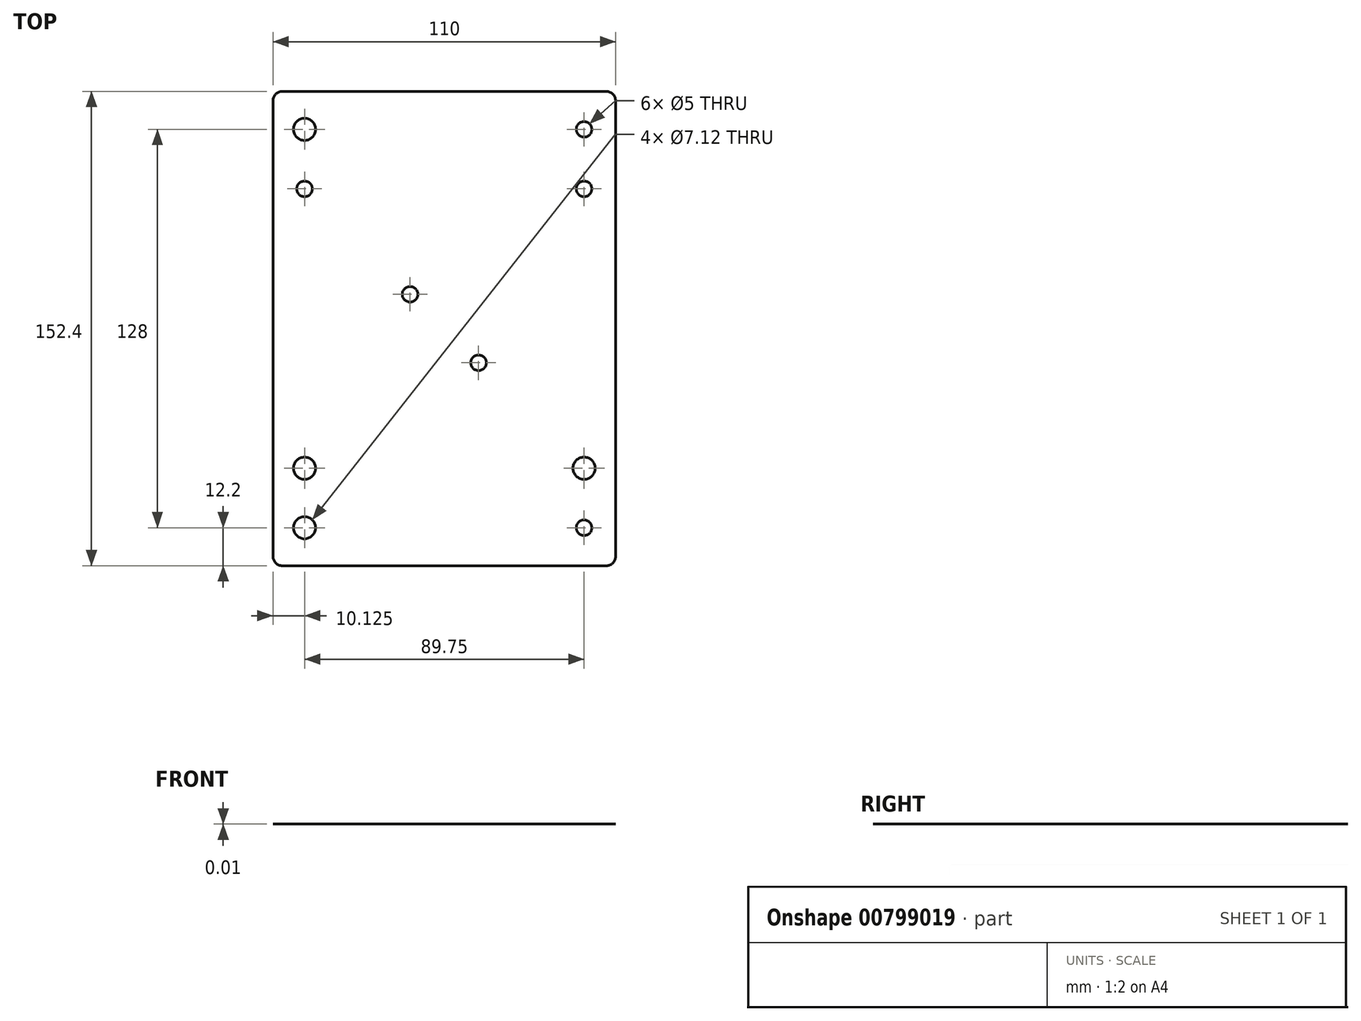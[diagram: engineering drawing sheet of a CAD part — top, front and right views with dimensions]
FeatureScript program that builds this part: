
annotation { "Feature Type Name" : "Feature", "Feature Type Description" : "" }
export const myFeature = defineFeature(function(context is Context, id is Id, definition is map)
    precondition{}
    {
        {
            var Q0;
            Q0=qCreatedBy(makeId("Top.planeOp"),FACE);
            var sketch = newSketch(context, id + "F0", { "sketchPlane" : qUnion([Q0])});
            skCircle(sketch, "E0", {"center": v(-11, 11) * mm, "radius": 2.5 * mm});
            skCircle(sketch, "E1", {"center": v(-44.87, 44.88) * mm, "radius": 2.5 * mm});
            skCircle(sketch, "E2", {"center": v(-44.87, -44.88) * mm, "radius": 3.56 * mm});
            skCircle(sketch, "E3", {"center": v(44.88, 64) * mm, "radius": 2.5 * mm});
            skCircle(sketch, "E4", {"center": v(-44.88, 64) * mm, "radius": 3.56 * mm});
            skLineSegment(sketch, "E5", {"start": v(52, 76.2) * mm, "end": v(-52, 76.2) * mm});
            skArc(sketch, "E6", {"start": v(-52, 76.2) * mm, "mid": v(-54.12, 75.32) * mm, "end": v(-55, 73.2) * mm});
            skLineSegment(sketch, "E7", {"start": v(-55, 73.2) * mm, "end": v(-55, -73.2) * mm});
            skArc(sketch, "E8", {"start": v(-55, -73.2) * mm, "mid": v(-54.12, -75.32) * mm, "end": v(-52, -76.2) * mm});
            skLineSegment(sketch, "E9", {"start": v(-52, -76.2) * mm, "end": v(52, -76.2) * mm});
            skArc(sketch, "E10", {"start": v(52, -76.2) * mm, "mid": v(54.12, -75.32) * mm, "end": v(55, -73.2) * mm});
            skLineSegment(sketch, "E11", {"start": v(55, -73.2) * mm, "end": v(55, 73.2) * mm});
            skArc(sketch, "E12", {"start": v(55, 73.2) * mm, "mid": v(54.12, 75.32) * mm, "end": v(52, 76.2) * mm});
            skCircle(sketch, "E13", {"center": v(-44.87, -64) * mm, "radius": 3.56 * mm});
            skCircle(sketch, "E14", {"center": v(44.88, -64) * mm, "radius": 2.5 * mm});
            skCircle(sketch, "E15", {"center": v(44.88, -44.88) * mm, "radius": 3.56 * mm});
            skCircle(sketch, "E16", {"center": v(44.88, 44.88) * mm, "radius": 2.5 * mm});
            skCircle(sketch, "E17", {"center": v(11, -11) * mm, "radius": 2.5 * mm});
            skLineSegment(sketch, "E18", {"start": v(-44.88, 64) * mm, "end": v(-44.87, 44.88) * mm, "construction": true});
            skLineSegment(sketch, "E19", {"start": v(-44.87, -44.88) * mm, "end": v(-44.87, 44.88) * mm, "construction": true});
            skLineSegment(sketch, "E20", {"start": v(-44.87, -44.88) * mm, "end": v(-44.87, -64) * mm, "construction": true});
            skLineSegment(sketch, "E21", {"start": v(-44.87, -64) * mm, "end": v(-44.87, -76.2) * mm, "construction": true});
            skLineSegment(sketch, "E22", {"start": v(-44.88, 64) * mm, "end": v(-44.88, 76.2) * mm, "construction": true});
            skLineSegment(sketch, "E23", {"start": v(44.88, 44.88) * mm, "end": v(44.88, -44.88) * mm, "construction": true});
            skLineSegment(sketch, "E24", {"start": v(44.88, -64) * mm, "end": v(44.88, -44.88) * mm, "construction": true});
            skLineSegment(sketch, "E25", {"start": v(44.88, -64) * mm, "end": v(44.88, -76.2) * mm, "construction": true});
            skLineSegment(sketch, "E26", {"start": v(-44.87, -64) * mm, "end": v(44.88, -64) * mm, "construction": true});
            skLineSegment(sketch, "E27", {"start": v(44.88, -64) * mm, "end": v(55, -64) * mm, "construction": true});
            skLineSegment(sketch, "E28", {"start": v(-44.87, -64) * mm, "end": v(-55, -64) * mm, "construction": true});
            skLineSegment(sketch, "E29", {"start": v(-44.87, -44.88) * mm, "end": v(-55, -44.88) * mm, "construction": true});
            skLineSegment(sketch, "E30", {"start": v(-44.87, -44.88) * mm, "end": v(44.88, -44.88) * mm, "construction": true});
            skLineSegment(sketch, "E31", {"start": v(44.88, -44.88) * mm, "end": v(55, -44.88) * mm, "construction": true});
            skLineSegment(sketch, "E32", {"start": v(11, -11) * mm, "end": v(55, -11) * mm, "construction": true});
            skLineSegment(sketch, "E33", {"start": v(11, -11) * mm, "end": v(-55, -11) * mm, "construction": true});
            skLineSegment(sketch, "E34", {"start": v(-11, 11) * mm, "end": v(55, 11) * mm, "construction": true});
            skLineSegment(sketch, "E35", {"start": v(-11, 11) * mm, "end": v(-55, 11) * mm, "construction": true});
            skLineSegment(sketch, "E36", {"start": v(-44.87, 44.88) * mm, "end": v(44.88, 44.88) * mm, "construction": true});
            skLineSegment(sketch, "E37", {"start": v(44.88, 44.88) * mm, "end": v(55, 44.88) * mm, "construction": true});
            skLineSegment(sketch, "E38", {"start": v(-44.87, 44.88) * mm, "end": v(-55, 44.87) * mm, "construction": true});
            skLineSegment(sketch, "E39", {"start": v(-44.88, 64) * mm, "end": v(44.88, 64) * mm, "construction": true});
            skLineSegment(sketch, "E40", {"start": v(44.88, 64) * mm, "end": v(55, 64) * mm, "construction": true});
            skLineSegment(sketch, "E41", {"start": v(-44.88, 64) * mm, "end": v(-55, 64) * mm, "construction": true});
            skLineSegment(sketch, "E42", {"start": v(-11, 11) * mm, "end": v(-11, 76.2) * mm, "construction": true});
            skLineSegment(sketch, "E43", {"start": v(-11, 11) * mm, "end": v(-11, -76.2) * mm, "construction": true});
            skLineSegment(sketch, "E44", {"start": v(11, -11) * mm, "end": v(11, -76.2) * mm, "construction": true});
            skLineSegment(sketch, "E45", {"start": v(11, -11) * mm, "end": v(11, 76.2) * mm, "construction": true});
            skLineSegment(sketch, "E46", {"start": v(-11, 11) * mm, "end": v(11, -11) * mm, "construction": true});
            skPoint(sketch, "E47", {"position": v(0, 0) * mm});
            skLineSegment(sketch, "E48", {"start": v(44.88, 64) * mm, "end": v(44.88, 76.2) * mm, "construction": true});
            skLineSegment(sketch, "E49", {"start": v(44.88, 64) * mm, "end": v(44.88, 44.88) * mm, "construction": true});
            skSolve(sketch);
        }
        {
            var Q0;
            Q0=qSketchRegion(id+"F0",true);
            extrude(context, id + "F1", {"entities" : qUnion([Q0]), "depth" : 1 / 101.6 * mm, "offsetDistance" : 25 * mm});
        }
    });
